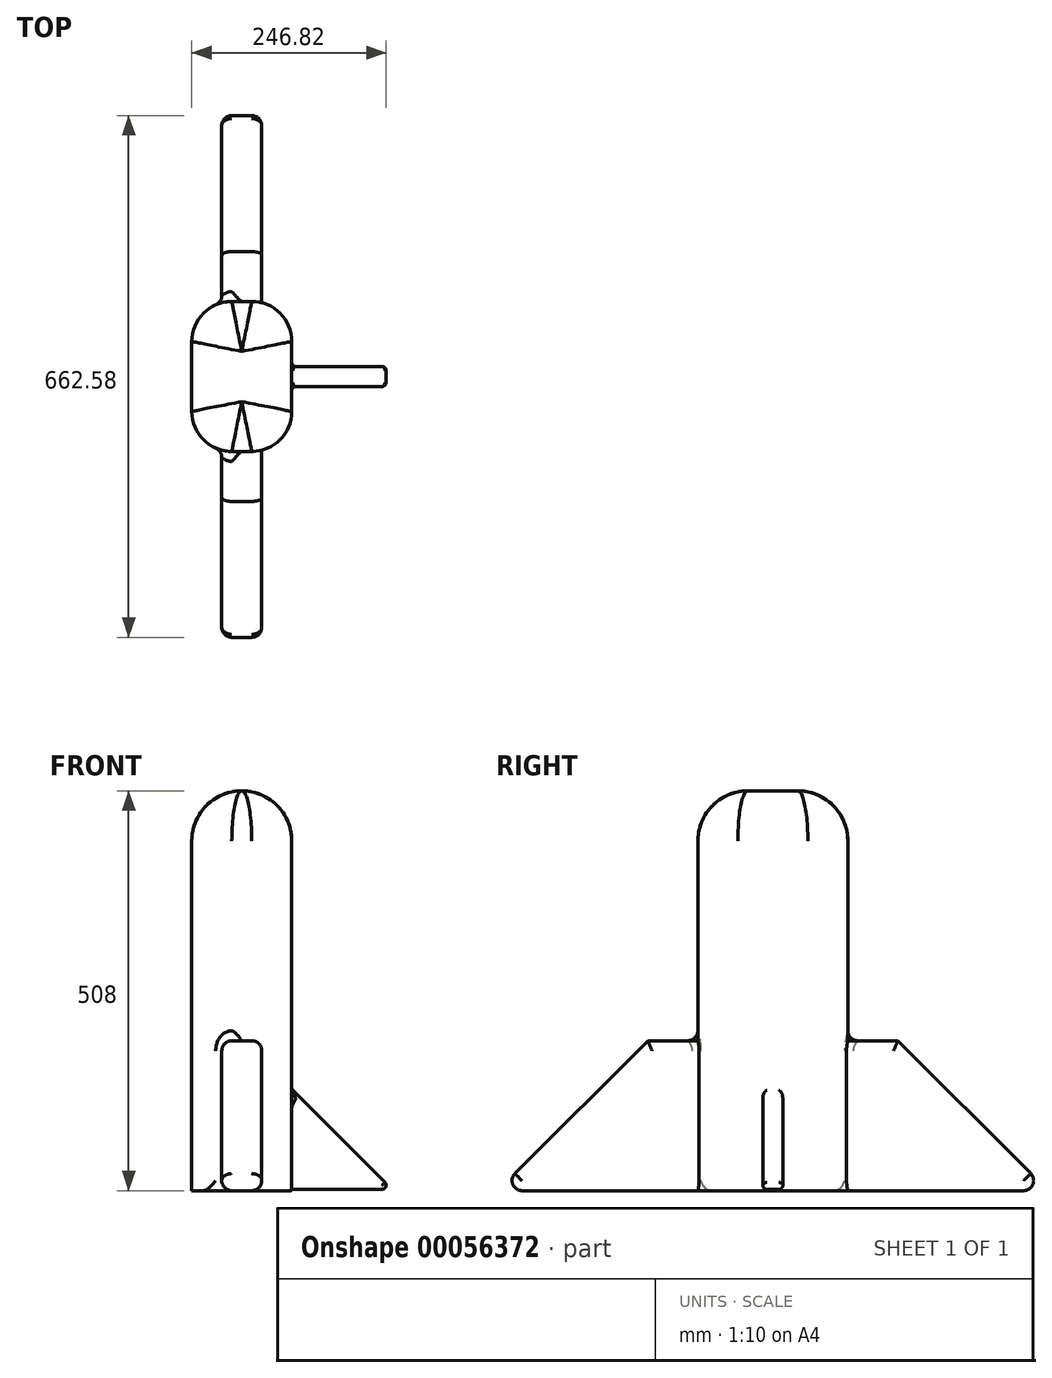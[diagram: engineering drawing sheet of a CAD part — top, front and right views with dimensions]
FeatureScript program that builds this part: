
annotation { "Feature Type Name" : "Feature", "Feature Type Description" : "" }
export const myFeature = defineFeature(function(context is Context, id is Id, definition is map)
    precondition{}
    {
        {
            var Q0;
            Q0=qCreatedBy(makeId("Right.planeOp"),FACE);
            var sketch = newSketch(context, id + "F0", { "sketchPlane" : qUnion([Q0])});
            skLineSegment(sketch, "E0.rect.bottom", {"start": v(95.25, -254) * mm, "end": v(-95.25, -254) * mm});
            skLineSegment(sketch, "E0.rect.top", {"start": v(95.25, 254) * mm, "end": v(-95.25, 254) * mm});
            skLineSegment(sketch, "E0.rect.left", {"start": v(95.25, -254) * mm, "end": v(95.25, 254) * mm});
            skLineSegment(sketch, "E0.rect.right", {"start": v(-95.25, -254) * mm, "end": v(-95.25, 254) * mm});
            skPoint(sketch, "E0.rect.middle", {"position": v(0, 0) * mm});
            skSolve(sketch);
        }
        {
            var Q0;
            Q0=makeQuery(id+"F0.imprint","IMPRINT",FACE,{"disambiguationData":[TD([[makeQuery(id+"F0.imprint","IMPRINT",EDGE,{"derivedFrom":sQuery(id+"F0.wireOp",EDGE,"E0.rect.bottom")}),-1.0]])]});
            extrude(context, id + "F1", {"entities" : qUnion([Q0]), "depth" : 127 * mm});
        }
        {
            var Q0;
            Q0=makeQuery(id+"F1.opExtrude","SWEPT_FACE",FACE,{"disambiguationData":[OSD([sQuery(id+"F0.wireOp",EDGE,"E0.rect.left")])]});
            var sketch = newSketch(context, id + "F2", { "sketchPlane" : qUnion([Q0])});
            skLineSegment(sketch, "E1.bottom", {"start": v(-88.9, -254) * mm, "end": v(-38.1, -254) * mm});
            skLineSegment(sketch, "E1.top", {"start": v(-88.9, -63.5) * mm, "end": v(-38.1, -63.5) * mm});
            skLineSegment(sketch, "E1.left", {"start": v(-88.9, -254) * mm, "end": v(-88.9, -63.5) * mm});
            skLineSegment(sketch, "E1.right", {"start": v(-38.1, -254) * mm, "end": v(-38.1, -63.5) * mm});
            skSolve(sketch);
        }
        {
            var Q0;
            Q0=makeQuery(id+"F2.imprint","IMPRINT",FACE,{"disambiguationData":[TD([[makeQuery(id+"F2.imprint","IMPRINT",EDGE,{"derivedFrom":sQuery(id+"F2.wireOp",EDGE,"E1.bottom")}),1.0]])]});
            extrude(context, id + "F3", {"entities" : qUnion([Q0]), "operationType" : NewBodyOperationType.ADD, "depth" : 317.5 * mm});
        }
        {
            var Q0;
            Q0=makeQuery(id+"F3.opExtrude","CAP_EDGE",EDGE,{"disambiguationData":[OSD([sQuery(id+"F2.wireOp",EDGE,"E1.top")])],"isStart":false});
            chamfer(context, id + "F4", {"entities" : qUnion([Q0]), "width" : 254 * mm, "tangentPropagation" : true});
        }
        {
            var Q0;
            Q0=makeQuery(id+"F1.opExtrude","SWEPT_FACE",FACE,{"disambiguationData":[OSD([sQuery(id+"F0.wireOp",EDGE,"E0.rect.right")])]});
            var sketch = newSketch(context, id + "F5", { "sketchPlane" : qUnion([Q0])});
            skLineSegment(sketch, "E2.bottom", {"start": v(88.9, -254) * mm, "end": v(38.1, -254) * mm});
            skLineSegment(sketch, "E2.top", {"start": v(88.9, -63.5) * mm, "end": v(38.1, -63.5) * mm});
            skLineSegment(sketch, "E2.left", {"start": v(88.9, -254) * mm, "end": v(88.9, -63.5) * mm});
            skLineSegment(sketch, "E2.right", {"start": v(38.1, -254) * mm, "end": v(38.1, -63.5) * mm});
            skSolve(sketch);
        }
        {
            var Q0;
            Q0=makeQuery(id+"F5.imprint","IMPRINT",FACE,{"disambiguationData":[TD([[makeQuery(id+"F5.imprint","IMPRINT",EDGE,{"derivedFrom":sQuery(id+"F5.wireOp",EDGE,"E2.bottom")}),-1.0]])]});
            extrude(context, id + "F6", {"entities" : qUnion([Q0]), "operationType" : NewBodyOperationType.ADD, "depth" : 317.5 * mm});
        }
        {
            var Q0;
            Q0=makeQuery(id+"F6.opExtrude","CAP_EDGE",EDGE,{"disambiguationData":[OSD([sQuery(id+"F5.wireOp",EDGE,"E2.top")])],"isStart":false});
            chamfer(context, id + "F7", {"entities" : qUnion([Q0]), "width" : 254 * mm, "tangentPropagation" : true});
        }
        {
            var Q0;
            Q0=makeQuery(id+"F1.opExtrude","CAP_FACE",FACE,{"disambiguationData":[OSD([sQuery(id+"F0.wireOp",EDGE,"E0.rect.bottom"),sQuery(id+"F0.wireOp",EDGE,"E0.rect.top"),sQuery(id+"F0.wireOp",EDGE,"E0.rect.left"),sQuery(id+"F0.wireOp",EDGE,"E0.rect.right")])],"isStart":false});
            var sketch = newSketch(context, id + "F8", { "sketchPlane" : qUnion([Q0])});
            skLineSegment(sketch, "E3.rect.bottom", {"start": v(12.7, -125.3) * mm, "end": v(-12.7, -125.3) * mm});
            skLineSegment(sketch, "E3.rect.top", {"start": v(12.7, -252.3) * mm, "end": v(-12.7, -252.3) * mm});
            skLineSegment(sketch, "E3.rect.left", {"start": v(12.7, -125.3) * mm, "end": v(12.7, -252.3) * mm});
            skLineSegment(sketch, "E3.rect.right", {"start": v(-12.7, -125.3) * mm, "end": v(-12.7, -252.3) * mm});
            skPoint(sketch, "E3.rect.middle", {"position": v(0, -188.8) * mm});
            skSolve(sketch);
        }
        {
            var Q0;
            Q0=makeQuery(id+"F8.imprint","IMPRINT",FACE,{"disambiguationData":[TD([[makeQuery(id+"F8.imprint","IMPRINT",EDGE,{"derivedFrom":sQuery(id+"F8.wireOp",EDGE,"E3.rect.bottom")}),1.0]])]});
            extrude(context, id + "F9", {"entities" : qUnion([Q0]), "operationType" : NewBodyOperationType.ADD, "depth" : 190.5 * mm});
        }
        {
            var Q0;
            Q0=makeQuery(id+"F9.opExtrude","CAP_EDGE",EDGE,{"disambiguationData":[OSD([sQuery(id+"F8.wireOp",EDGE,"E3.rect.bottom")])],"isStart":false});
            chamfer(context, id + "F10", {"entities" : qUnion([Q0]), "width" : 190.5 * mm, "tangentPropagation" : true});
        }
        {
            var Q0;
            Q0=makeQuery(id+"F10.opChamfer","BLEND_FACE",FACE,{"disambiguationData":[OSD([sQuery(id+"F8.wireOp",EDGE,"E3.rect.bottom")])]});
            fillet(context, id + "F11", {"entities" : qUnion([Q0]), "radius" : 5.08 * mm, "tangentPropagation" : true, "allowEdgeOverflow" : false});
        }
        {
            var Q0;
            Q0=makeQuery(id+"F1.opExtrude","CAP_EDGE",EDGE,{"disambiguationData":[OSD([sQuery(id+"F0.wireOp",EDGE,"E0.rect.left")])],"isStart":false});
            var Q1;
            Q1=makeQuery(id+"F1.opExtrude","CAP_EDGE",EDGE,{"disambiguationData":[OSD([sQuery(id+"F0.wireOp",EDGE,"E0.rect.left")])],"isStart":true});
            var Q2;
            Q2=makeQuery(id+"F1.opExtrude","CAP_EDGE",EDGE,{"disambiguationData":[OSD([sQuery(id+"F0.wireOp",EDGE,"E0.rect.right")])],"isStart":true});
            var Q3;
            Q3=makeQuery(id+"F1.opExtrude","CAP_EDGE",EDGE,{"disambiguationData":[OSD([sQuery(id+"F0.wireOp",EDGE,"E0.rect.right")])],"isStart":false});
            fillet(context, id + "F12", {"entities" : qUnion([Q0, Q1, Q2, Q3]), "radius" : 50.8 * mm, "tangentPropagation" : true, "allowEdgeOverflow" : false});
        }
        {
            var Q0;
            Q0=makeQuery(id+"F3.opExtrude","SWEPT_FACE",FACE,{"disambiguationData":[OSD([sQuery(id+"F2.wireOp",EDGE,"E1.right")])]});
            var Q1;
            Q1=makeQuery(id+"F6.opExtrude","SWEPT_FACE",FACE,{"disambiguationData":[OSD([sQuery(id+"F5.wireOp",EDGE,"E2.right")])]});
            fillet(context, id + "F13", {"entities" : qUnion([Q0, Q1]), "radius" : 12.7 * mm, "tangentPropagation" : true, "allowEdgeOverflow" : false});
        }
        {
            var Q0;
            Q0=makeQuery(id+"F6.opExtrude","SWEPT_EDGE",EDGE,{"disambiguationData":[OSD([sQuery(id+"F5.wireOp",EDGE,"E2.top"),sQuery(id+"F5.wireOp",EDGE,"E2.left")])]});
            var Q1;
            Q1=makeQuery(id+"F7.opChamfer","BLEND_EDGE",EDGE,{"blendedFrom":[makeQuery(id+"F6.opExtrude","CAP_EDGE",EDGE,{"disambiguationData":[OSD([sQuery(id+"F5.wireOp",EDGE,"E2.top")])],"isStart":false}),makeQuery(id+"F6.opExtrude","SWEPT_FACE",FACE,{"disambiguationData":[OSD([sQuery(id+"F5.wireOp",EDGE,"E2.left")])]})],"blendedInto":[makeQuery(id+"F6.opExtrude","SWEPT_FACE",FACE,{"disambiguationData":[OSD([sQuery(id+"F5.wireOp",EDGE,"E2.left")])]})]});
            var Q2;
            Q2=makeQuery(id+"F6.opExtrude","SWEPT_EDGE",EDGE,{"disambiguationData":[OSD([sQuery(id+"F0.wireOp",EDGE,"E0.rect.bottom"),sQuery(id+"F0.wireOp",EDGE,"E0.rect.right"),sQuery(id+"F5.wireOp",EDGE,"E2.bottom"),sQuery(id+"F5.wireOp",EDGE,"E2.left")])]});
            var Q3;
            Q3=makeQuery(id+"F3.opExtrude","SWEPT_EDGE",EDGE,{"disambiguationData":[OSD([sQuery(id+"F0.wireOp",EDGE,"E0.rect.bottom"),sQuery(id+"F0.wireOp",EDGE,"E0.rect.left"),sQuery(id+"F2.wireOp",EDGE,"E1.bottom"),sQuery(id+"F2.wireOp",EDGE,"E1.left")])]});
            var Q4;
            Q4=makeQuery(id+"F4.opChamfer","BLEND_EDGE",EDGE,{"blendedFrom":[makeQuery(id+"F3.opExtrude","CAP_EDGE",EDGE,{"disambiguationData":[OSD([sQuery(id+"F2.wireOp",EDGE,"E1.top")])],"isStart":false}),makeQuery(id+"F3.opExtrude","SWEPT_FACE",FACE,{"disambiguationData":[OSD([sQuery(id+"F2.wireOp",EDGE,"E1.left")])]})],"blendedInto":[makeQuery(id+"F3.opExtrude","SWEPT_FACE",FACE,{"disambiguationData":[OSD([sQuery(id+"F2.wireOp",EDGE,"E1.left")])]})]});
            var Q5;
            Q5=makeQuery(id+"F3.opExtrude","SWEPT_EDGE",EDGE,{"disambiguationData":[OSD([sQuery(id+"F2.wireOp",EDGE,"E1.top"),sQuery(id+"F2.wireOp",EDGE,"E1.left")])]});
            fillet(context, id + "F14", {"entities" : qUnion([Q0, Q1, Q2, Q3, Q4, Q5]), "radius" : 12.7 * mm, "tangentPropagation" : true, "allowEdgeOverflow" : false});
        }
        {
            var Q0;
            Q0=makeQuery(id+"F4.opChamfer","BLEND_EDGE",EDGE,{"blendedFrom":[makeQuery(id+"F3.opExtrude","CAP_EDGE",EDGE,{"disambiguationData":[OSD([sQuery(id+"F2.wireOp",EDGE,"E1.top")])],"isStart":false}),makeQuery(id+"F3.boolean.opBoolean","MERGE",FACE,{"derivedFrom":[makeQuery(id+"F1.opExtrude","SWEPT_FACE",FACE,{"disambiguationData":[OSD([sQuery(id+"F0.wireOp",EDGE,"E0.rect.bottom")])]}),makeQuery(id+"F3.opExtrude","SWEPT_FACE",FACE,{"disambiguationData":[OSD([sQuery(id+"F2.wireOp",EDGE,"E1.bottom")])]})]})],"blendedInto":[makeQuery(id+"F3.boolean.opBoolean","MERGE",FACE,{"derivedFrom":[makeQuery(id+"F1.opExtrude","SWEPT_FACE",FACE,{"disambiguationData":[OSD([sQuery(id+"F0.wireOp",EDGE,"E0.rect.bottom")])]}),makeQuery(id+"F3.opExtrude","SWEPT_FACE",FACE,{"disambiguationData":[OSD([sQuery(id+"F2.wireOp",EDGE,"E1.bottom")])]})]})]});
            var Q1;
            Q1=makeQuery(id+"F7.opChamfer","BLEND_EDGE",EDGE,{"blendedFrom":[makeQuery(id+"F6.opExtrude","CAP_EDGE",EDGE,{"disambiguationData":[OSD([sQuery(id+"F5.wireOp",EDGE,"E2.top")])],"isStart":false}),makeQuery(id+"F6.boolean.opBoolean","MERGE",FACE,{"derivedFrom":[makeQuery(id+"F3.boolean.opBoolean","MERGE",FACE,{"derivedFrom":[makeQuery(id+"F1.opExtrude","SWEPT_FACE",FACE,{"disambiguationData":[OSD([sQuery(id+"F0.wireOp",EDGE,"E0.rect.bottom")])]}),makeQuery(id+"F3.opExtrude","SWEPT_FACE",FACE,{"disambiguationData":[OSD([sQuery(id+"F2.wireOp",EDGE,"E1.bottom")])]})]}),makeQuery(id+"F6.opExtrude","SWEPT_FACE",FACE,{"disambiguationData":[OSD([sQuery(id+"F5.wireOp",EDGE,"E2.bottom")])]})]})],"blendedInto":[makeQuery(id+"F6.boolean.opBoolean","MERGE",FACE,{"derivedFrom":[makeQuery(id+"F3.boolean.opBoolean","MERGE",FACE,{"derivedFrom":[makeQuery(id+"F1.opExtrude","SWEPT_FACE",FACE,{"disambiguationData":[OSD([sQuery(id+"F0.wireOp",EDGE,"E0.rect.bottom")])]}),makeQuery(id+"F3.opExtrude","SWEPT_FACE",FACE,{"disambiguationData":[OSD([sQuery(id+"F2.wireOp",EDGE,"E1.bottom")])]})]}),makeQuery(id+"F6.opExtrude","SWEPT_FACE",FACE,{"disambiguationData":[OSD([sQuery(id+"F5.wireOp",EDGE,"E2.bottom")])]})]})]});
            fillet(context, id + "F15", {"entities" : qUnion([Q0, Q1]), "radius" : 12.7 * mm, "tangentPropagation" : true, "allowEdgeOverflow" : false});
        }
        {
            var Q0;
            Q0=makeQuery(id+"F12.opFillet","BLEND_EDGE",EDGE,{"blendedFrom":[makeQuery(id+"F1.opExtrude","CAP_EDGE",EDGE,{"disambiguationData":[OSD([sQuery(id+"F0.wireOp",EDGE,"E0.rect.right")])],"isStart":false}),makeQuery(id+"F6.boolean.opBoolean","MERGE",FACE,{"derivedFrom":[makeQuery(id+"F3.boolean.opBoolean","MERGE",FACE,{"derivedFrom":[makeQuery(id+"F1.opExtrude","SWEPT_FACE",FACE,{"disambiguationData":[OSD([sQuery(id+"F0.wireOp",EDGE,"E0.rect.bottom")])]}),makeQuery(id+"F3.opExtrude","SWEPT_FACE",FACE,{"disambiguationData":[OSD([sQuery(id+"F2.wireOp",EDGE,"E1.bottom")])]})]}),makeQuery(id+"F6.opExtrude","SWEPT_FACE",FACE,{"disambiguationData":[OSD([sQuery(id+"F5.wireOp",EDGE,"E2.bottom")])]})]})],"blendedInto":[makeQuery(id+"F6.boolean.opBoolean","MERGE",FACE,{"derivedFrom":[makeQuery(id+"F3.boolean.opBoolean","MERGE",FACE,{"derivedFrom":[makeQuery(id+"F1.opExtrude","SWEPT_FACE",FACE,{"disambiguationData":[OSD([sQuery(id+"F0.wireOp",EDGE,"E0.rect.bottom")])]}),makeQuery(id+"F3.opExtrude","SWEPT_FACE",FACE,{"disambiguationData":[OSD([sQuery(id+"F2.wireOp",EDGE,"E1.bottom")])]})]}),makeQuery(id+"F6.opExtrude","SWEPT_FACE",FACE,{"disambiguationData":[OSD([sQuery(id+"F5.wireOp",EDGE,"E2.bottom")])]})]})]});
            var Q1;
            Q1=makeQuery(id+"F1.opExtrude","CAP_EDGE",EDGE,{"disambiguationData":[OSD([sQuery(id+"F0.wireOp",EDGE,"E0.rect.bottom")])],"isStart":false});
            var Q2;
            Q2=makeQuery(id+"F12.opFillet","BLEND_EDGE",EDGE,{"blendedFrom":[makeQuery(id+"F1.opExtrude","CAP_EDGE",EDGE,{"disambiguationData":[OSD([sQuery(id+"F0.wireOp",EDGE,"E0.rect.left")])],"isStart":false}),makeQuery(id+"F6.boolean.opBoolean","MERGE",FACE,{"derivedFrom":[makeQuery(id+"F3.boolean.opBoolean","MERGE",FACE,{"derivedFrom":[makeQuery(id+"F1.opExtrude","SWEPT_FACE",FACE,{"disambiguationData":[OSD([sQuery(id+"F0.wireOp",EDGE,"E0.rect.bottom")])]}),makeQuery(id+"F3.opExtrude","SWEPT_FACE",FACE,{"disambiguationData":[OSD([sQuery(id+"F2.wireOp",EDGE,"E1.bottom")])]})]}),makeQuery(id+"F6.opExtrude","SWEPT_FACE",FACE,{"disambiguationData":[OSD([sQuery(id+"F5.wireOp",EDGE,"E2.bottom")])]})]})],"blendedInto":[makeQuery(id+"F6.boolean.opBoolean","MERGE",FACE,{"derivedFrom":[makeQuery(id+"F3.boolean.opBoolean","MERGE",FACE,{"derivedFrom":[makeQuery(id+"F1.opExtrude","SWEPT_FACE",FACE,{"disambiguationData":[OSD([sQuery(id+"F0.wireOp",EDGE,"E0.rect.bottom")])]}),makeQuery(id+"F3.opExtrude","SWEPT_FACE",FACE,{"disambiguationData":[OSD([sQuery(id+"F2.wireOp",EDGE,"E1.bottom")])]})]}),makeQuery(id+"F6.opExtrude","SWEPT_FACE",FACE,{"disambiguationData":[OSD([sQuery(id+"F5.wireOp",EDGE,"E2.bottom")])]})]})]});
            fillet(context, id + "F16", {"entities" : qUnion([Q0, Q1, Q2]), "radius" : 1.33 * mm, "allowEdgeOverflow" : false});
        }
        {
            var Q0;
            Q0=makeQuery(id+"F9.opExtrude","SWEPT_EDGE",EDGE,{"disambiguationData":[OSD([sQuery(id+"F8.wireOp",EDGE,"E3.rect.top"),sQuery(id+"F8.wireOp",EDGE,"E3.rect.right")])]});
            var Q1;
            Q1=makeQuery(id+"F9.opExtrude","SWEPT_EDGE",EDGE,{"disambiguationData":[OSD([sQuery(id+"F8.wireOp",EDGE,"E3.rect.top"),sQuery(id+"F8.wireOp",EDGE,"E3.rect.left")])]});
            fillet(context, id + "F17", {"entities" : qUnion([Q0, Q1]), "radius" : 5.08 * mm, "tangentPropagation" : true, "allowEdgeOverflow" : false});
        }
        {
            var Q0;
            Q0=makeQuery(id+"F1.opExtrude","SWEPT_FACE",FACE,{"disambiguationData":[OSD([sQuery(id+"F0.wireOp",EDGE,"E0.rect.top")])]});
            fillet(context, id + "F18", {"entities" : qUnion([Q0]), "radius" : 63.5 * mm, "tangentPropagation" : true, "allowEdgeOverflow" : false});
        }
    });
